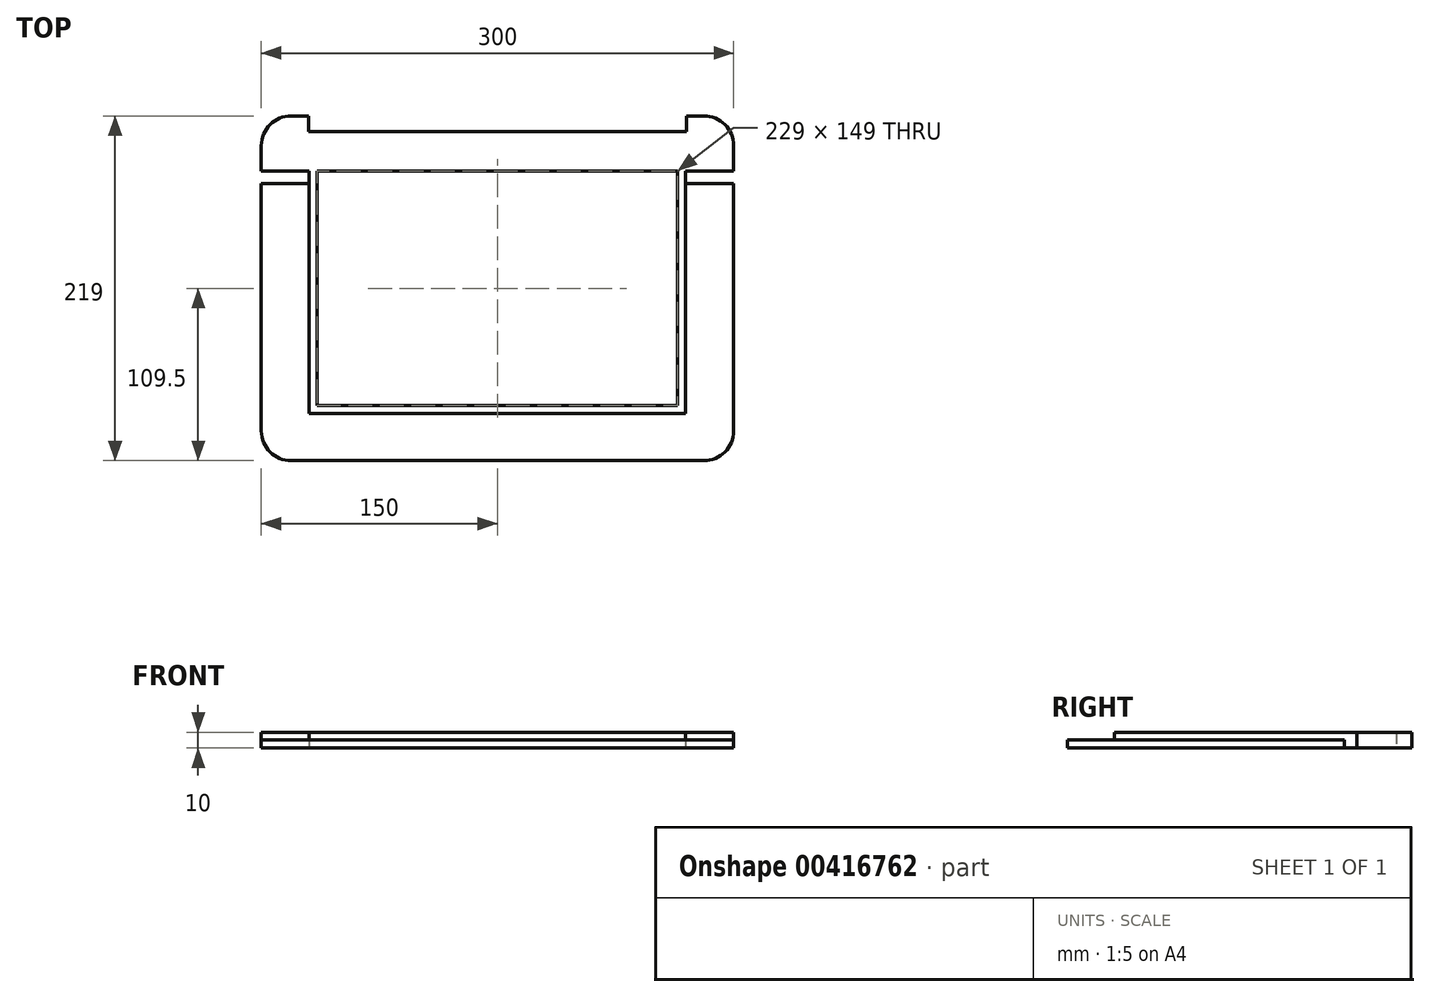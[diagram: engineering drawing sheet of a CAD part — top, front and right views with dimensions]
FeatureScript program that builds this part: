
annotation { "Feature Type Name" : "Feature", "Feature Type Description" : "" }
export const myFeature = defineFeature(function(context is Context, id is Id, definition is map)
    precondition{}
    {
        {
            var Q0;
            Q0=qCreatedBy(makeId("Top.planeOp"),FACE);
            var sketch = newSketch(context, id + "F0", { "sketchPlane" : qUnion([Q0])});
            skLineSegment(sketch, "E0.bottom", {"start": v(0, 0) * mm, "end": v(30, 0) * mm});
            skLineSegment(sketch, "E0.top", {"start": v(0, -219) * mm, "end": v(300, -219) * mm});
            skLineSegment(sketch, "E0.left", {"start": v(0, 0) * mm, "end": v(0, -219) * mm});
            skLineSegment(sketch, "E0.right", {"start": v(300, 0) * mm, "end": v(300, -219) * mm});
            skLineSegment(sketch, "E1.bottom", {"start": v(264.5, -35) * mm, "end": v(35.5, -35) * mm});
            skLineSegment(sketch, "E1.top", {"start": v(264.5, -184) * mm, "end": v(35.5, -184) * mm});
            skLineSegment(sketch, "E1.left", {"start": v(264.5, -35) * mm, "end": v(264.5, -184) * mm});
            skLineSegment(sketch, "E1.right", {"start": v(35.5, -35) * mm, "end": v(35.5, -184) * mm});
            skPoint(sketch, "E1.middle", {"position": v(150, -109.5) * mm});
            skLineSegment(sketch, "E2", {"start": v(150, -10) * mm, "end": v(270, -10) * mm});
            skLineSegment(sketch, "E3", {"start": v(270, -10) * mm, "end": v(270, 0) * mm});
            skLineSegment(sketch, "E4.MirrorCS", {"start": v(150, -10) * mm, "end": v(30, -10) * mm});
            skLineSegment(sketch, "E5.MirrorCS", {"start": v(30, -10) * mm, "end": v(30, 0) * mm});
            skLineSegment(sketch, "E6.trimOffspring", {"start": v(270, 0) * mm, "end": v(300, 0) * mm});
            skLineSegment(sketch, "E7.0", {"start": v(30.5, -35) * mm, "end": v(30.5, -184) * mm});
            skLineSegment(sketch, "E8.0", {"start": v(264.5, -189) * mm, "end": v(35.5, -189) * mm});
            skLineSegment(sketch, "E9.0", {"start": v(269.5, -35) * mm, "end": v(269.5, -184) * mm});
            skLineSegment(sketch, "E10", {"start": v(30.5, -35) * mm, "end": v(0, -35) * mm});
            skLineSegment(sketch, "E11", {"start": v(269.5, -35) * mm, "end": v(300, -35) * mm});
            skLineSegment(sketch, "E12", {"start": v(269.5, -184) * mm, "end": v(269.5, -189) * mm});
            skLineSegment(sketch, "E13", {"start": v(269.5, -189) * mm, "end": v(264.5, -189) * mm});
            skLineSegment(sketch, "E14", {"start": v(35.5, -189) * mm, "end": v(30.5, -189) * mm});
            skLineSegment(sketch, "E15", {"start": v(30.5, -189) * mm, "end": v(30.5, -184) * mm});
            skLineSegment(sketch, "E16", {"start": v(30.5, -35) * mm, "end": v(30.5, -43) * mm});
            skLineSegment(sketch, "E17", {"start": v(30.5, -43) * mm, "end": v(0, -43) * mm});
            skLineSegment(sketch, "E18", {"start": v(269.5, -43) * mm, "end": v(300, -43) * mm});
            skSolve(sketch);
        }
        {
            var Q0;
            {var subQ11=sQuery(id+"F0.wireOp",EDGE,"E0.bottom");Q0=makeQuery(id+"F0.imprint","IMPRINT",FACE,{"disambiguationData":[TD([[makeQuery(id+"F0.imprint","IMPRINT",EDGE,{"derivedFrom":subQ11}),-1.0]])]});}
            extrude(context, id + "F1", {"entities" : qUnion([Q0]), "depth" : 10 * mm});
        }
        {
            var Q0;
            {var subQ1=sQuery(id+"F0.wireOp",EDGE,"E0.top");Q0=makeQuery(id+"F0.imprint","IMPRINT",FACE,{"disambiguationData":[TD([[makeQuery(id+"F0.imprint","IMPRINT",EDGE,{"derivedFrom":subQ1}),1.0]])]});}
            extrude(context, id + "F2", {"entities" : qUnion([Q0]), "operationType" : NewBodyOperationType.ADD, "depth" : 5 * mm});
        }
        {
            var Q0;
            Q0=makeQuery(id+"F1.opExtrude","SWEPT_EDGE",EDGE,{"disambiguationData":[OSD([sQuery(id+"F0.wireOp",EDGE,"E0.bottom"),sQuery(id+"F0.wireOp",EDGE,"E0.left")])]});
            var Q1;
            Q1=makeQuery(id+"F1.opExtrude","SWEPT_EDGE",EDGE,{"disambiguationData":[OSD([sQuery(id+"F0.wireOp",EDGE,"E0.right"),sQuery(id+"F0.wireOp",EDGE,"E6.trimOffspring")])]});
            var Q2;
            Q2=makeQuery(id+"F2.opExtrude","SWEPT_EDGE",EDGE,{"disambiguationData":[OSD([sQuery(id+"F0.wireOp",EDGE,"E0.top"),sQuery(id+"F0.wireOp",EDGE,"E0.right")])]});
            var Q3;
            Q3=makeQuery(id+"F2.opExtrude","SWEPT_EDGE",EDGE,{"disambiguationData":[OSD([sQuery(id+"F0.wireOp",EDGE,"E0.top"),sQuery(id+"F0.wireOp",EDGE,"E0.left")])]});
            fillet(context, id + "F3", {"entities" : qUnion([Q0, Q1, Q2, Q3]), "radius" : 19 * mm, "tangentPropagation" : true, "allowEdgeOverflow" : false});
        }
    });
